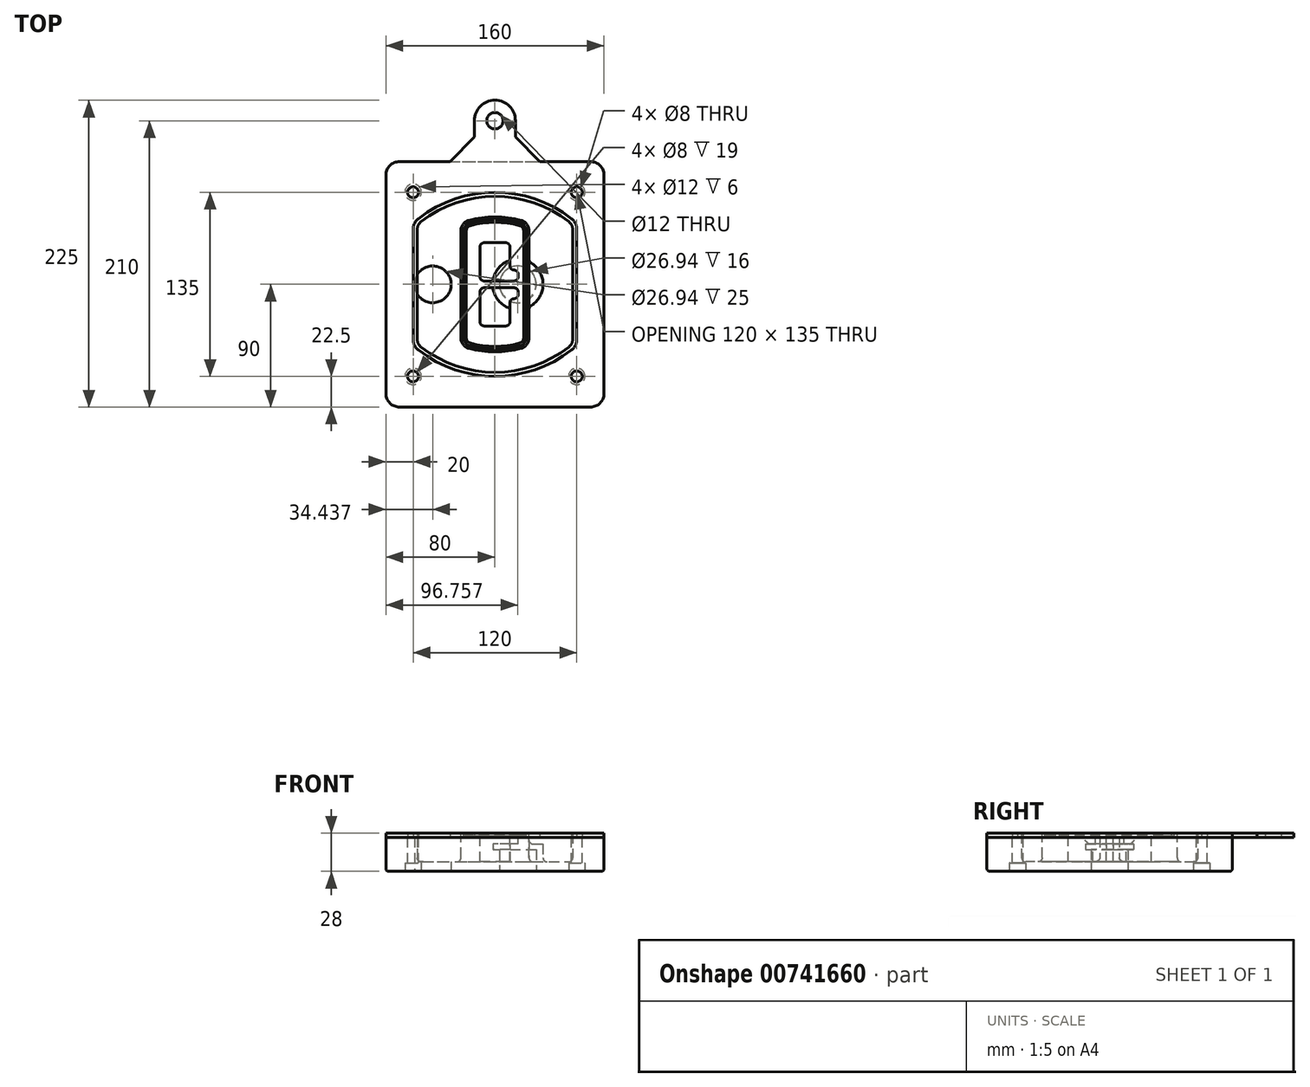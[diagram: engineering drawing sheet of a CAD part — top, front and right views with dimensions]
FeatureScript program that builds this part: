
annotation { "Feature Type Name" : "Feature", "Feature Type Description" : "" }
export const myFeature = defineFeature(function(context is Context, id is Id, definition is map)
    precondition{}
    {
        {
            var Q0;
            Q0=qCreatedBy(makeId("Top.planeOp"),FACE);
            var sketch = newSketch(context, id + "F0", { "sketchPlane" : qUnion([Q0])});
            skPoint(sketch, "E0.rect.middle", {"position": v(0, 0) * mm});
            skLineSegment(sketch, "E1.bottom", {"start": v(-70, -90) * mm, "end": v(70, -90) * mm});
            skLineSegment(sketch, "E1.top", {"start": v(-70, 90) * mm, "end": v(70, 90) * mm});
            skLineSegment(sketch, "E1.left", {"start": v(-80, -80) * mm, "end": v(-80, 80) * mm});
            skLineSegment(sketch, "E1.right", {"start": v(80, -80) * mm, "end": v(80, 80) * mm});
            skLineSegment(sketch, "E2", {"start": v(-80, 90) * mm, "end": v(80, -90) * mm, "construction": true});
            skLineSegment(sketch, "E3", {"start": v(80, 90) * mm, "end": v(-80, -90) * mm, "construction": true});
            skCircle(sketch, "E4", {"center": v(-60, 67.5) * mm, "radius": 4 * mm});
            skCircle(sketch, "E5", {"center": v(60, 67.5) * mm, "radius": 4 * mm});
            skCircle(sketch, "E6", {"center": v(60, -67.5) * mm, "radius": 4 * mm});
            skCircle(sketch, "E7", {"center": v(-60, -67.5) * mm, "radius": 4 * mm});
            skLineSegment(sketch, "E8", {"start": v(-60, 67.5) * mm, "end": v(60, 67.5) * mm, "construction": true});
            skLineSegment(sketch, "E9", {"start": v(60, 67.5) * mm, "end": v(60, -67.5) * mm, "construction": true});
            skLineSegment(sketch, "E10", {"start": v(60, -67.5) * mm, "end": v(-60, -67.5) * mm, "construction": true});
            skLineSegment(sketch, "E11", {"start": v(-60, -67.5) * mm, "end": v(-60, 67.5) * mm, "construction": true});
            skLineSegment(sketch, "E12", {"start": v(-60, 40.3) * mm, "end": v(-60, -40.3) * mm});
            skLineSegment(sketch, "E13", {"start": v(60, 40.3) * mm, "end": v(60, -40.3) * mm});
            skArc(sketch, "E14", {"start": v(56.15, 48.18) * mm, "mid": v(0, 67.5) * mm, "end": v(-56.15, 48.18) * mm});
            skArc(sketch, "E15", {"start": v(-56.15, -48.18) * mm, "mid": v(0, -67.5) * mm, "end": v(56.15, -48.18) * mm});
            skLineSegment(sketch, "E16", {"start": v(-60, 0) * mm, "end": v(60, 0) * mm, "construction": true});
            skPoint(sketch, "E17.visualSharp", {"position": v(-60, -45) * mm});
            skArc(sketch, "E17.filletArc", {"start": v(-60, -40.3) * mm, "mid": v(-58.99, -44.68) * mm, "end": v(-56.15, -48.18) * mm});
            skPoint(sketch, "E18.visualSharp", {"position": v(-60, 45) * mm});
            skArc(sketch, "E18.filletArc", {"start": v(-56.15, 48.18) * mm, "mid": v(-58.99, 44.68) * mm, "end": v(-60, 40.3) * mm});
            skPoint(sketch, "E19.visualSharp", {"position": v(60, 45) * mm});
            skArc(sketch, "E19.filletArc", {"start": v(60, 40.3) * mm, "mid": v(58.99, 44.68) * mm, "end": v(56.15, 48.18) * mm});
            skPoint(sketch, "E20.visualSharp", {"position": v(60, -45) * mm});
            skArc(sketch, "E20.filletArc", {"start": v(56.15, -48.18) * mm, "mid": v(58.99, -44.68) * mm, "end": v(60, -40.3) * mm});
            skPoint(sketch, "E21.visualSharp", {"position": v(-80, 90) * mm});
            skArc(sketch, "E21.filletArc", {"start": v(-70, 90) * mm, "mid": v(-77.07, 87.07) * mm, "end": v(-80, 80) * mm});
            skPoint(sketch, "E22.visualSharp", {"position": v(80, 90) * mm});
            skArc(sketch, "E22.filletArc", {"start": v(80, 80) * mm, "mid": v(77.07, 87.07) * mm, "end": v(70, 90) * mm});
            skPoint(sketch, "E23.visualSharp", {"position": v(80, -90) * mm});
            skArc(sketch, "E23.filletArc", {"start": v(70, -90) * mm, "mid": v(77.07, -87.07) * mm, "end": v(80, -80) * mm});
            skPoint(sketch, "E24.visualSharp", {"position": v(-80, -90) * mm});
            skArc(sketch, "E24.filletArc", {"start": v(-80, -80) * mm, "mid": v(-77.07, -87.07) * mm, "end": v(-70, -90) * mm});
            skArc(sketch, "E25.0", {"start": v(57, 40.3) * mm, "mid": v(56.3, 43.36) * mm, "end": v(54.3, 45.81) * mm});
            skLineSegment(sketch, "E25.1", {"start": v(57, 40.3) * mm, "end": v(57, -40.3) * mm});
            skArc(sketch, "E25.2", {"start": v(54.3, -45.81) * mm, "mid": v(56.3, -43.36) * mm, "end": v(57, -40.3) * mm});
            skArc(sketch, "E25.3", {"start": v(-54.3, -45.81) * mm, "mid": v(0, -64.5) * mm, "end": v(54.3, -45.81) * mm});
            skArc(sketch, "E25.4", {"start": v(-57, -40.3) * mm, "mid": v(-56.3, -43.36) * mm, "end": v(-54.3, -45.81) * mm});
            skArc(sketch, "E25.5", {"start": v(54.3, 45.81) * mm, "mid": v(0, 64.5) * mm, "end": v(-54.3, 45.81) * mm});
            skLineSegment(sketch, "E25.6", {"start": v(-57, 40.3) * mm, "end": v(-57, -40.3) * mm});
            skArc(sketch, "E25.7", {"start": v(-54.3, 45.81) * mm, "mid": v(-56.3, 43.36) * mm, "end": v(-57, 40.3) * mm});
            skArc(sketch, "E26.0", {"start": v(-58.62, 51.33) * mm, "mid": v(-62.58, 46.43) * mm, "end": v(-64, 40.3) * mm});
            skArc(sketch, "E26.1", {"start": v(58.62, 51.33) * mm, "mid": v(0, 71.5) * mm, "end": v(-58.62, 51.33) * mm});
            skArc(sketch, "E26.2", {"start": v(64, 40.3) * mm, "mid": v(62.58, 46.43) * mm, "end": v(58.62, 51.33) * mm});
            skLineSegment(sketch, "E26.3", {"start": v(64, 40.3) * mm, "end": v(64, -40.3) * mm});
            skArc(sketch, "E26.4", {"start": v(58.62, -51.33) * mm, "mid": v(62.58, -46.43) * mm, "end": v(64, -40.3) * mm});
            skLineSegment(sketch, "E26.5", {"start": v(-64, 40.3) * mm, "end": v(-64, -40.3) * mm});
            skArc(sketch, "E26.6", {"start": v(-58.62, -51.33) * mm, "mid": v(0, -71.5) * mm, "end": v(58.62, -51.33) * mm});
            skArc(sketch, "E26.7", {"start": v(-64, -40.3) * mm, "mid": v(-62.58, -46.43) * mm, "end": v(-58.62, -51.33) * mm});
            skSolve(sketch);
        }
        {
            var Q0;
            Q0=makeQuery(id+"F0.imprint","IMPRINT",FACE,{"disambiguationData":[TD([[makeQuery(id+"F0.imprint","IMPRINT",EDGE,{"derivedFrom":sQuery(id+"F0.wireOp",EDGE,"E1.bottom")}),1.0]])]});
            var Q1;
            Q1=makeQuery(id+"F0.imprint","IMPRINT",FACE,{"disambiguationData":[TD([[makeQuery(id+"F0.imprint","IMPRINT",EDGE,{"derivedFrom":sQuery(id+"F0.wireOp",EDGE,"E12")}),1.0]])]});
            var Q2;
            Q2=makeQuery(id+"F0.imprint","IMPRINT",FACE,{"disambiguationData":[TD([[makeQuery(id+"F0.imprint","IMPRINT",EDGE,{"derivedFrom":sQuery(id+"F0.wireOp",EDGE,"E25.0")}),1.0]])]});
            var Q3;
            Q3=makeQuery(id+"F0.imprint","IMPRINT",FACE,{"disambiguationData":[TD([[makeQuery(id+"F0.imprint","IMPRINT",EDGE,{"derivedFrom":sQuery(id+"F0.wireOp",EDGE,"E12")}),-1.0]])]});
            extrude(context, id + "F1", {"entities" : qUnion([Q0, Q1, Q2, Q3]), "oppositeDirection" : true, "depth" : 25 * mm});
        }
        {
            var Q0;
            Q0=makeQuery(id+"F0.imprint","IMPRINT",FACE,{"disambiguationData":[TD([[makeQuery(id+"F0.imprint","IMPRINT",EDGE,{"derivedFrom":sQuery(id+"F0.wireOp",EDGE,"E12")}),1.0]])]});
            extrude(context, id + "F2", {"entities" : qUnion([Q0]), "operationType" : NewBodyOperationType.ADD, "depth" : 3 * mm});
        }
        {
            var Q0;
            Q0=makeQuery(id+"F0.imprint","IMPRINT",FACE,{"disambiguationData":[TD([[makeQuery(id+"F0.imprint","IMPRINT",EDGE,{"derivedFrom":sQuery(id+"F0.wireOp",EDGE,"E25.0")}),1.0]])]});
            extrude(context, id + "F3", {"entities" : qUnion([Q0]), "operationType" : NewBodyOperationType.REMOVE, "oppositeDirection" : true, "depth" : 18 * mm});
        }
        {
            var Q0;
            Q0=makeQuery(id+"F2.opExtrude","CAP_FACE",FACE,{"disambiguationData":[OSD([sQuery(id+"F0.wireOp",EDGE,"E12"),sQuery(id+"F0.wireOp",EDGE,"E13"),sQuery(id+"F0.wireOp",EDGE,"E14"),sQuery(id+"F0.wireOp",EDGE,"E15"),sQuery(id+"F0.wireOp",EDGE,"E17.filletArc"),sQuery(id+"F0.wireOp",EDGE,"E18.filletArc"),sQuery(id+"F0.wireOp",EDGE,"E19.filletArc"),sQuery(id+"F0.wireOp",EDGE,"E20.filletArc"),sQuery(id+"F0.wireOp",EDGE,"E25.0"),sQuery(id+"F0.wireOp",EDGE,"E25.1"),sQuery(id+"F0.wireOp",EDGE,"E25.2"),sQuery(id+"F0.wireOp",EDGE,"E25.3"),sQuery(id+"F0.wireOp",EDGE,"E25.4"),sQuery(id+"F0.wireOp",EDGE,"E25.5"),sQuery(id+"F0.wireOp",EDGE,"E25.6"),sQuery(id+"F0.wireOp",EDGE,"E25.7")])],"isStart":false});
            var sketch = newSketch(context, id + "F4", { "sketchPlane" : qUnion([Q0])});
            skArc(sketch, "E27.0", {"start": v(-19.08, -46.97) * mm, "mid": v(0, -49.5) * mm, "end": v(19.08, -46.97) * mm});
            skArc(sketch, "E28.0", {"start": v(19.08, 46.97) * mm, "mid": v(0, 49.5) * mm, "end": v(-19.08, 46.97) * mm});
            skLineSegment(sketch, "E29", {"start": v(-25, 39.25) * mm, "end": v(-25, -39.25) * mm});
            skLineSegment(sketch, "E30", {"start": v(25, 39.25) * mm, "end": v(25, -39.25) * mm});
            skLineSegment(sketch, "E31", {"start": v(-25, 45.1) * mm, "end": v(25, 45.1) * mm, "construction": true});
            skLineSegment(sketch, "E32", {"start": v(-25, -45.1) * mm, "end": v(25, -45.1) * mm, "construction": true});
            skPoint(sketch, "E33.visualSharp", {"position": v(-25, 45.1) * mm});
            skArc(sketch, "E33.filletArc", {"start": v(-19.08, 46.97) * mm, "mid": v(-23.35, 44.11) * mm, "end": v(-25, 39.25) * mm});
            skPoint(sketch, "E34.visualSharp", {"position": v(25, 45.1) * mm});
            skArc(sketch, "E34.filletArc", {"start": v(25, 39.25) * mm, "mid": v(23.35, 44.11) * mm, "end": v(19.08, 46.97) * mm});
            skPoint(sketch, "E35.visualSharp", {"position": v(25, -45.1) * mm});
            skArc(sketch, "E35.filletArc", {"start": v(19.08, -46.97) * mm, "mid": v(23.35, -44.11) * mm, "end": v(25, -39.25) * mm});
            skPoint(sketch, "E36.visualSharp", {"position": v(-25, -45.1) * mm});
            skArc(sketch, "E36.filletArc", {"start": v(-25, -39.25) * mm, "mid": v(-23.35, -44.11) * mm, "end": v(-19.08, -46.97) * mm});
            skArc(sketch, "E37.0", {"start": v(54.3, 45.81) * mm, "mid": v(0, 64.5) * mm, "end": v(-54.3, 45.81) * mm});
            skArc(sketch, "E37.1", {"start": v(-54.3, 45.81) * mm, "mid": v(-56.3, 43.36) * mm, "end": v(-57, 40.3) * mm});
            skLineSegment(sketch, "E37.2", {"start": v(-57, 40.3) * mm, "end": v(-57, -40.3) * mm});
            skArc(sketch, "E37.3", {"start": v(-57, -40.3) * mm, "mid": v(-56.3, -43.36) * mm, "end": v(-54.3, -45.81) * mm});
            skArc(sketch, "E37.4", {"start": v(-54.3, -45.81) * mm, "mid": v(0, -64.5) * mm, "end": v(54.3, -45.81) * mm});
            skArc(sketch, "E37.5", {"start": v(54.3, -45.81) * mm, "mid": v(56.3, -43.36) * mm, "end": v(57, -40.3) * mm});
            skLineSegment(sketch, "E37.6", {"start": v(57, 40.3) * mm, "end": v(57, -40.3) * mm});
            skArc(sketch, "E37.7", {"start": v(57, 40.3) * mm, "mid": v(56.3, 43.36) * mm, "end": v(54.3, 45.81) * mm});
            skLineSegment(sketch, "E38.0", {"start": v(23, 39.25) * mm, "end": v(23, -39.25) * mm});
            skArc(sketch, "E38.1", {"start": v(18.56, -45.04) * mm, "mid": v(21.76, -42.9) * mm, "end": v(23, -39.25) * mm});
            skArc(sketch, "E38.2", {"start": v(-18.56, -45.04) * mm, "mid": v(0, -47.5) * mm, "end": v(18.56, -45.04) * mm});
            skArc(sketch, "E38.3", {"start": v(-23, -39.25) * mm, "mid": v(-21.76, -42.9) * mm, "end": v(-18.56, -45.04) * mm});
            skLineSegment(sketch, "E38.4", {"start": v(-23, 39.25) * mm, "end": v(-23, -39.25) * mm});
            skArc(sketch, "E38.5", {"start": v(23, 39.25) * mm, "mid": v(21.76, 42.9) * mm, "end": v(18.56, 45.04) * mm});
            skArc(sketch, "E38.6", {"start": v(-18.56, 45.04) * mm, "mid": v(-21.76, 42.9) * mm, "end": v(-23, 39.25) * mm});
            skArc(sketch, "E38.7", {"start": v(18.56, 45.04) * mm, "mid": v(0, 47.5) * mm, "end": v(-18.56, 45.04) * mm});
            skArc(sketch, "E39.0", {"start": v(21, 39.25) * mm, "mid": v(20.18, 41.68) * mm, "end": v(18.04, 43.1) * mm});
            skLineSegment(sketch, "E39.1", {"start": v(21, 39.25) * mm, "end": v(21, -39.25) * mm});
            skArc(sketch, "E39.2", {"start": v(18.04, -43.1) * mm, "mid": v(20.18, -41.68) * mm, "end": v(21, -39.25) * mm});
            skArc(sketch, "E39.3", {"start": v(-18.04, -43.1) * mm, "mid": v(0, -45.5) * mm, "end": v(18.04, -43.1) * mm});
            skArc(sketch, "E39.4", {"start": v(-21, -39.25) * mm, "mid": v(-20.18, -41.68) * mm, "end": v(-18.04, -43.1) * mm});
            skArc(sketch, "E39.5", {"start": v(18.04, 43.1) * mm, "mid": v(0, 45.5) * mm, "end": v(-18.04, 43.1) * mm});
            skLineSegment(sketch, "E39.6", {"start": v(-21, 39.25) * mm, "end": v(-21, -39.25) * mm});
            skArc(sketch, "E39.7", {"start": v(-18.04, 43.1) * mm, "mid": v(-20.18, 41.68) * mm, "end": v(-21, 39.25) * mm});
            skLineSegment(sketch, "E40", {"start": v(-25, 0) * mm, "end": v(25, 0) * mm, "construction": true});
            skLineSegment(sketch, "E41", {"start": v(-11, 5.5) * mm, "end": v(-11, 27.5) * mm});
            skLineSegment(sketch, "E42", {"start": v(-8, 30.5) * mm, "end": v(8, 30.5) * mm});
            skLineSegment(sketch, "E43", {"start": v(11, 27.5) * mm, "end": v(11, 13.5) * mm});
            skLineSegment(sketch, "E44", {"start": v(14, 10.5) * mm, "end": v(14, 10.5) * mm});
            skLineSegment(sketch, "E45", {"start": v(17, 7.5) * mm, "end": v(17, 5.5) * mm});
            skLineSegment(sketch, "E46", {"start": v(14, 2.5) * mm, "end": v(-8, 2.5) * mm});
            skPoint(sketch, "E47.visualSharp", {"position": v(-11, 30.5) * mm});
            skArc(sketch, "E47.filletArc", {"start": v(-8, 30.5) * mm, "mid": v(-10.12, 29.62) * mm, "end": v(-11, 27.5) * mm});
            skPoint(sketch, "E48.visualSharp", {"position": v(11, 30.5) * mm});
            skArc(sketch, "E48.filletArc", {"start": v(11, 27.5) * mm, "mid": v(10.12, 29.62) * mm, "end": v(8, 30.5) * mm});
            skPoint(sketch, "E49.visualSharp", {"position": v(11, 10.5) * mm});
            skArc(sketch, "E49.filletArc", {"start": v(11, 13.5) * mm, "mid": v(11.88, 11.38) * mm, "end": v(14, 10.5) * mm});
            skPoint(sketch, "E50.visualSharp", {"position": v(17, 10.5) * mm});
            skArc(sketch, "E50.filletArc", {"start": v(17, 7.5) * mm, "mid": v(16.12, 9.62) * mm, "end": v(14, 10.5) * mm});
            skPoint(sketch, "E51.visualSharp", {"position": v(17, 2.5) * mm});
            skArc(sketch, "E51.filletArc", {"start": v(14, 2.5) * mm, "mid": v(16.12, 3.38) * mm, "end": v(17, 5.5) * mm});
            skPoint(sketch, "E52.visualSharp", {"position": v(-11, 2.5) * mm});
            skArc(sketch, "E52.filletArc", {"start": v(-11, 5.5) * mm, "mid": v(-10.12, 3.38) * mm, "end": v(-8, 2.5) * mm});
            skLineSegment(sketch, "E53.0.MirrorCS", {"start": v(14, -2.5) * mm, "end": v(-8, -2.5) * mm});
            skArc(sketch, "E54.0.MirrorCS", {"start": v(-11, -5.5) * mm, "mid": v(-10.12, -3.38) * mm, "end": v(-8, -2.5) * mm});
            skLineSegment(sketch, "E55.0.MirrorCS", {"start": v(-11, -5.5) * mm, "end": v(-11, -27.5) * mm});
            skArc(sketch, "E56.0.MirrorCS", {"start": v(-8, -30.5) * mm, "mid": v(-10.12, -29.62) * mm, "end": v(-11, -27.5) * mm});
            skLineSegment(sketch, "E57.0.MirrorCS", {"start": v(-8, -30.5) * mm, "end": v(8, -30.5) * mm});
            skArc(sketch, "E58.0.MirrorCS", {"start": v(11, -27.5) * mm, "mid": v(10.12, -29.62) * mm, "end": v(8, -30.5) * mm});
            skLineSegment(sketch, "E59.0.MirrorCS", {"start": v(11, -27.5) * mm, "end": v(11, -13.5) * mm});
            skArc(sketch, "E60.0.MirrorCS", {"start": v(11, -13.5) * mm, "mid": v(11.88, -11.38) * mm, "end": v(14, -10.5) * mm});
            skArc(sketch, "E61.0.MirrorCS", {"start": v(17, -7.5) * mm, "mid": v(16.12, -9.62) * mm, "end": v(14, -10.5) * mm});
            skLineSegment(sketch, "E62.0.MirrorCS", {"start": v(17, -7.5) * mm, "end": v(17, -5.5) * mm});
            skArc(sketch, "E63.0.MirrorCS", {"start": v(14, -2.5) * mm, "mid": v(16.12, -3.38) * mm, "end": v(17, -5.5) * mm});
            skSolve(sketch);
        }
        {
            var Q0;
            Q0=makeQuery(id+"F4.imprint","IMPRINT",FACE,{"disambiguationData":[TD([[makeQuery(id+"F4.imprint","IMPRINT",EDGE,{"derivedFrom":sQuery(id+"F4.wireOp",EDGE,"E27.0")}),1.0]])]});
            var Q1;
            Q1=makeQuery(id+"F4.imprint","IMPRINT",FACE,{"disambiguationData":[TD([[makeQuery(id+"F4.imprint","IMPRINT",EDGE,{"derivedFrom":sQuery(id+"F4.wireOp",EDGE,"E38.0")}),-1.0]])]});
            var Q2;
            Q2=makeQuery(id+"F4.imprint","IMPRINT",FACE,{"disambiguationData":[TD([[makeQuery(id+"F4.imprint","IMPRINT",EDGE,{"derivedFrom":sQuery(id+"F4.wireOp",EDGE,"E39.0")}),1.0]])]});
            extrude(context, id + "F5", {"entities" : qUnion([Q0, Q1, Q2]), "operationType" : NewBodyOperationType.ADD, "endBound" : BoundingType.UP_TO_NEXT, "oppositeDirection" : true, "depth" : 25 * mm});
        }
        {
            var Q0;
            Q0=makeQuery(id+"F4.imprint","IMPRINT",FACE,{"disambiguationData":[TD([[makeQuery(id+"F4.imprint","IMPRINT",EDGE,{"derivedFrom":sQuery(id+"F4.wireOp",EDGE,"E38.0")}),-1.0]])]});
            extrude(context, id + "F6", {"entities" : qUnion([Q0]), "operationType" : NewBodyOperationType.REMOVE, "oppositeDirection" : true, "depth" : 2 * mm});
        }
        {
            var Q0;
            Q0=makeQuery(id+"F1.opExtrude","CAP_FACE",FACE,{"disambiguationData":[OSD([sQuery(id+"F0.wireOp",EDGE,"E1.bottom"),sQuery(id+"F0.wireOp",EDGE,"E1.top"),sQuery(id+"F0.wireOp",EDGE,"E1.left"),sQuery(id+"F0.wireOp",EDGE,"E1.right"),sQuery(id+"F0.wireOp",EDGE,"E4"),sQuery(id+"F0.wireOp",EDGE,"E5"),sQuery(id+"F0.wireOp",EDGE,"E6"),sQuery(id+"F0.wireOp",EDGE,"E7"),sQuery(id+"F0.wireOp",EDGE,"E21.filletArc"),sQuery(id+"F0.wireOp",EDGE,"E22.filletArc"),sQuery(id+"F0.wireOp",EDGE,"E23.filletArc"),sQuery(id+"F0.wireOp",EDGE,"E24.filletArc")])],"isStart":false});
            var sketch = newSketch(context, id + "F7", { "sketchPlane" : qUnion([Q0])});
            skCircle(sketch, "E64", {"center": v(16.76, 0) * mm, "radius": 13.47 * mm});
            skCircle(sketch, "E65", {"center": v(-45.56, 0) * mm, "radius": 13.47 * mm});
            skLineSegment(sketch, "E66", {"start": v(80, 0) * mm, "end": v(-80, 0) * mm});
            skCircle(sketch, "E67", {"center": v(16.76, 0) * mm, "radius": 18.47 * mm});
            skCircle(sketch, "E68", {"center": v(60, -67.5) * mm, "radius": 6 * mm});
            skCircle(sketch, "E69", {"center": v(-60, -67.5) * mm, "radius": 6 * mm});
            skCircle(sketch, "E70", {"center": v(-60, 67.5) * mm, "radius": 6 * mm});
            skCircle(sketch, "E71", {"center": v(60, 67.5) * mm, "radius": 6 * mm});
            skSolve(sketch);
        }
        {
            var Q0;
            {var subQ1=sQuery(id+"F7.wireOp",EDGE,"E66");var subQ4=sQuery(id+"F7.wireOp",EDGE,"E64");var subQ6=makeQuery(id+"F7.imprint","INTERSECT",VERTEX,{"disambiguationData":[OD(0.0)],"derivedFrom":[subQ4,subQ1]});Q0=makeQuery(id+"F7.imprint","IMPRINT",FACE,{"disambiguationData":[TD([[makeQuery(id+"F7.imprint","IMPRINT",EDGE,{"disambiguationData":[TD([[subQ6,-1.0]])],"derivedFrom":subQ4}),-1.0]])]});}
            var Q1;
            {var subQ0=sQuery(id+"F7.wireOp",EDGE,"E66");var subQ1=sQuery(id+"F7.wireOp",EDGE,"E64");var subQ3=makeQuery(id+"F7.imprint","INTERSECT",VERTEX,{"disambiguationData":[OD(0.0)],"derivedFrom":[subQ1,subQ0]});Q1=makeQuery(id+"F7.imprint","IMPRINT",FACE,{"disambiguationData":[TD([[makeQuery(id+"F7.imprint","IMPRINT",EDGE,{"disambiguationData":[TD([[subQ3,-1.0]])],"derivedFrom":subQ1}),1.0]])]});}
            var Q2;
            {var subQ0=sQuery(id+"F7.wireOp",EDGE,"E66");var subQ1=sQuery(id+"F7.wireOp",EDGE,"E64");var subQ3=makeQuery(id+"F7.imprint","INTERSECT",VERTEX,{"disambiguationData":[OD(0.0)],"derivedFrom":[subQ1,subQ0]});Q2=makeQuery(id+"F7.imprint","IMPRINT",FACE,{"disambiguationData":[TD([[makeQuery(id+"F7.imprint","IMPRINT",EDGE,{"disambiguationData":[TD([[subQ3,1.0]])],"derivedFrom":subQ1}),1.0]])]});}
            var Q3;
            {var subQ1=sQuery(id+"F7.wireOp",EDGE,"E66");var subQ4=sQuery(id+"F7.wireOp",EDGE,"E64");var subQ6=makeQuery(id+"F7.imprint","INTERSECT",VERTEX,{"disambiguationData":[OD(0.0)],"derivedFrom":[subQ4,subQ1]});Q3=makeQuery(id+"F7.imprint","IMPRINT",FACE,{"disambiguationData":[TD([[makeQuery(id+"F7.imprint","IMPRINT",EDGE,{"disambiguationData":[TD([[subQ6,1.0]])],"derivedFrom":subQ4}),-1.0]])]});}
            extrude(context, id + "F8", {"entities" : qUnion([Q0, Q1, Q2, Q3]), "operationType" : NewBodyOperationType.ADD, "oppositeDirection" : true, "depth" : 20 * mm});
        }
        {
            var Q0;
            {var subQ0=sQuery(id+"F7.wireOp",EDGE,"E66");var subQ1=sQuery(id+"F7.wireOp",EDGE,"E64");var subQ3=makeQuery(id+"F7.imprint","INTERSECT",VERTEX,{"disambiguationData":[OD(0.0)],"derivedFrom":[subQ1,subQ0]});Q0=makeQuery(id+"F7.imprint","IMPRINT",FACE,{"disambiguationData":[TD([[makeQuery(id+"F7.imprint","IMPRINT",EDGE,{"disambiguationData":[TD([[subQ3,-1.0]])],"derivedFrom":subQ1}),1.0]])]});}
            var Q1;
            {var subQ0=sQuery(id+"F7.wireOp",EDGE,"E66");var subQ1=sQuery(id+"F7.wireOp",EDGE,"E64");var subQ3=makeQuery(id+"F7.imprint","INTERSECT",VERTEX,{"disambiguationData":[OD(0.0)],"derivedFrom":[subQ1,subQ0]});Q1=makeQuery(id+"F7.imprint","IMPRINT",FACE,{"disambiguationData":[TD([[makeQuery(id+"F7.imprint","IMPRINT",EDGE,{"disambiguationData":[TD([[subQ3,1.0]])],"derivedFrom":subQ1}),1.0]])]});}
            extrude(context, id + "F9", {"entities" : qUnion([Q0, Q1]), "operationType" : NewBodyOperationType.REMOVE, "oppositeDirection" : true, "depth" : 16 * mm});
        }
        {
            var Q0;
            {var subQ0=sQuery(id+"F7.wireOp",EDGE,"E66");var subQ1=sQuery(id+"F7.wireOp",EDGE,"E65");var subQ3=makeQuery(id+"F7.imprint","INTERSECT",VERTEX,{"disambiguationData":[OD(0.0)],"derivedFrom":[subQ1,subQ0]});Q0=makeQuery(id+"F7.imprint","IMPRINT",FACE,{"disambiguationData":[TD([[makeQuery(id+"F7.imprint","IMPRINT",EDGE,{"disambiguationData":[TD([[subQ3,-1.0]])],"derivedFrom":subQ1}),1.0]])]});}
            var Q1;
            {var subQ0=sQuery(id+"F7.wireOp",EDGE,"E66");var subQ1=sQuery(id+"F7.wireOp",EDGE,"E65");var subQ3=makeQuery(id+"F7.imprint","INTERSECT",VERTEX,{"disambiguationData":[OD(0.0)],"derivedFrom":[subQ1,subQ0]});Q1=makeQuery(id+"F7.imprint","IMPRINT",FACE,{"disambiguationData":[TD([[makeQuery(id+"F7.imprint","IMPRINT",EDGE,{"disambiguationData":[TD([[subQ3,1.0]])],"derivedFrom":subQ1}),1.0]])]});}
            extrude(context, id + "F10", {"entities" : qUnion([Q0, Q1]), "operationType" : NewBodyOperationType.REMOVE, "oppositeDirection" : true, "depth" : 25 * mm});
        }
        {
            var Q0;
            Q0=makeQuery(id+"F7.imprint","IMPRINT",FACE,{"disambiguationData":[TD([[makeQuery(id+"F7.imprint","IMPRINT",EDGE,{"derivedFrom":sQuery(id+"F7.wireOp",EDGE,"E68")}),1.0]])]});
            var Q1;
            Q1=makeQuery(id+"F7.imprint","IMPRINT",FACE,{"disambiguationData":[TD([[makeQuery(id+"F7.imprint","IMPRINT",EDGE,{"derivedFrom":makeQuery(id+"F1.opExtrude","CAP_EDGE",EDGE,{"disambiguationData":[OSD([sQuery(id+"F0.wireOp",EDGE,"E5")])],"isStart":false})}),-1.0]])]});
            var Q2;
            Q2=makeQuery(id+"F7.imprint","IMPRINT",FACE,{"disambiguationData":[TD([[makeQuery(id+"F7.imprint","IMPRINT",EDGE,{"derivedFrom":sQuery(id+"F7.wireOp",EDGE,"E69")}),1.0]])]});
            var Q3;
            Q3=makeQuery(id+"F7.imprint","IMPRINT",FACE,{"disambiguationData":[TD([[makeQuery(id+"F7.imprint","IMPRINT",EDGE,{"derivedFrom":makeQuery(id+"F1.opExtrude","CAP_EDGE",EDGE,{"disambiguationData":[OSD([sQuery(id+"F0.wireOp",EDGE,"E4")])],"isStart":false})}),-1.0]])]});
            var Q4;
            Q4=makeQuery(id+"F7.imprint","IMPRINT",FACE,{"disambiguationData":[TD([[makeQuery(id+"F7.imprint","IMPRINT",EDGE,{"derivedFrom":sQuery(id+"F7.wireOp",EDGE,"E70")}),1.0]])]});
            var Q5;
            Q5=makeQuery(id+"F7.imprint","IMPRINT",FACE,{"disambiguationData":[TD([[makeQuery(id+"F7.imprint","IMPRINT",EDGE,{"derivedFrom":makeQuery(id+"F1.opExtrude","CAP_EDGE",EDGE,{"disambiguationData":[OSD([sQuery(id+"F0.wireOp",EDGE,"E7")])],"isStart":false})}),-1.0]])]});
            var Q6;
            Q6=makeQuery(id+"F7.imprint","IMPRINT",FACE,{"disambiguationData":[TD([[makeQuery(id+"F7.imprint","IMPRINT",EDGE,{"derivedFrom":sQuery(id+"F7.wireOp",EDGE,"E71")}),1.0]])]});
            var Q7;
            Q7=makeQuery(id+"F7.imprint","IMPRINT",FACE,{"disambiguationData":[TD([[makeQuery(id+"F7.imprint","IMPRINT",EDGE,{"derivedFrom":makeQuery(id+"F1.opExtrude","CAP_EDGE",EDGE,{"disambiguationData":[OSD([sQuery(id+"F0.wireOp",EDGE,"E6")])],"isStart":false})}),-1.0]])]});
            extrude(context, id + "F11", {"entities" : qUnion([Q0, Q1, Q2, Q3, Q4, Q5, Q6, Q7]), "operationType" : NewBodyOperationType.REMOVE, "oppositeDirection" : true, "depth" : 6 * mm});
        }
        {
            var Q0;
            Q0=makeQuery(id+"F9.boolean.opBoolean","COPY",FACE,{"derivedFrom":makeQuery(id+"F9.opExtrude","CAP_FACE",FACE,{"disambiguationData":[OSD([sQuery(id+"F7.wireOp",EDGE,"E64")])],"isStart":false})});
            var sketch = newSketch(context, id + "F12", { "sketchPlane" : qUnion([Q0])});
            skArc(sketch, "E72.0", {"start": v(11, 17.55) * mm, "mid": v(2.57, 11.82) * mm, "end": v(-1.54, 2.5) * mm});
            skArc(sketch, "E72.1", {"start": v(-1.54, -2.5) * mm, "mid": v(2.57, -11.82) * mm, "end": v(11, -17.55) * mm});
            skLineSegment(sketch, "E73", {"start": v(-1.54, -2.5) * mm, "end": v(14, -2.5) * mm});
            skLineSegment(sketch, "E74.0", {"start": v(14, 2.5) * mm, "end": v(-1.54, 2.5) * mm});
            skArc(sketch, "E74.1", {"start": v(14, 2.5) * mm, "mid": v(16.12, 3.38) * mm, "end": v(17, 5.5) * mm});
            skLineSegment(sketch, "E74.2", {"start": v(17, 7.5) * mm, "end": v(17, 5.5) * mm});
            skArc(sketch, "E74.3", {"start": v(17, 7.5) * mm, "mid": v(16.12, 9.62) * mm, "end": v(14, 10.5) * mm});
            skArc(sketch, "E74.4", {"start": v(11, 13.5) * mm, "mid": v(11.88, 11.38) * mm, "end": v(14, 10.5) * mm});
            skLineSegment(sketch, "E74.5", {"start": v(11, 17.55) * mm, "end": v(11, 13.5) * mm});
            skLineSegment(sketch, "E74.7", {"start": v(14, -2.5) * mm, "end": v(-1.54, -2.5) * mm});
            skArc(sketch, "E74.8", {"start": v(14, -2.5) * mm, "mid": v(16.12, -3.38) * mm, "end": v(17, -5.5) * mm});
            skLineSegment(sketch, "E74.9", {"start": v(17, -7.5) * mm, "end": v(17, -5.5) * mm});
            skArc(sketch, "E74.10", {"start": v(17, -7.5) * mm, "mid": v(16.12, -9.62) * mm, "end": v(14, -10.5) * mm});
            skArc(sketch, "E74.11", {"start": v(11, -13.5) * mm, "mid": v(11.88, -11.38) * mm, "end": v(14, -10.5) * mm});
            skLineSegment(sketch, "E74.12", {"start": v(11, -17.55) * mm, "end": v(11, -13.5) * mm});
            skPoint(sketch, "E75.orphan", {"position": v(11, -27.5) * mm});
            skPoint(sketch, "E76.orphan", {"position": v(-8, -2.5) * mm});
            skPoint(sketch, "E77.orphan", {"position": v(-8, 2.5) * mm});
            skPoint(sketch, "E78.orphan", {"position": v(11, 27.5) * mm});
            skSolve(sketch);
        }
        {
            var Q0;
            {var subQ7=sQuery(id+"F12.wireOp",EDGE,"E72.0");var subQ14=sQuery(id+"F12.wireOp",EDGE,"E72.1");var subQ16=sQuery(id+"F12.wireOp",EDGE,"E74.1");var subQ18=sQuery(id+"F12.wireOp",EDGE,"E74.8");Q0=qUnion([makeQuery(id+"F12.imprint","IMPRINT",FACE,{"disambiguationData":[TD([[makeQuery(id+"F12.imprint","IMPRINT",EDGE,{"derivedFrom":subQ7}),1.0]])]}),makeQuery(id+"F12.imprint","IMPRINT",FACE,{"disambiguationData":[TD([[makeQuery(id+"F12.imprint","IMPRINT",EDGE,{"derivedFrom":subQ14}),1.0]])]}),makeQuery(id+"F12.imprint","IMPRINT",FACE,{"disambiguationData":[TD([[makeQuery(id+"F12.imprint","IMPRINT",EDGE,{"derivedFrom":subQ16}),1.0]])]}),makeQuery(id+"F12.imprint","IMPRINT",FACE,{"disambiguationData":[TD([[makeQuery(id+"F12.imprint","IMPRINT",EDGE,{"derivedFrom":subQ18}),-1.0]])]})]);}
            var Q1;
            Q1=makeQuery(id+"F5.boolean.opBoolean","SPLIT",FACE,{"disambiguationData":[TD([makeQuery(id+"F5.opExtrude","SWEPT_FACE",FACE,{"disambiguationData":[OSD([sQuery(id+"F4.wireOp",EDGE,"E41")])]})])],"derivedFrom":makeQuery(id+"F3.boolean.opBoolean","COPY",FACE,{"derivedFrom":makeQuery(id+"F3.opExtrude","CAP_FACE",FACE,{"disambiguationData":[OSD([sQuery(id+"F0.wireOp",EDGE,"E25.0"),sQuery(id+"F0.wireOp",EDGE,"E25.1"),sQuery(id+"F0.wireOp",EDGE,"E25.2"),sQuery(id+"F0.wireOp",EDGE,"E25.3"),sQuery(id+"F0.wireOp",EDGE,"E25.4"),sQuery(id+"F0.wireOp",EDGE,"E25.5"),sQuery(id+"F0.wireOp",EDGE,"E25.6"),sQuery(id+"F0.wireOp",EDGE,"E25.7")])],"isStart":false})})});
            extrude(context, id + "F13", {"entities" : qUnion([Q0]), "operationType" : NewBodyOperationType.REMOVE, "endBound" : BoundingType.UP_TO_SURFACE, "endBoundEntityFace" : qUnion([Q1]), "depth" : 25 * mm});
        }
        {
            var Q0;
            Q0=makeQuery(id+"F3.boolean.opBoolean","COPY",EDGE,{"derivedFrom":makeQuery(id+"F3.opExtrude","CAP_EDGE",EDGE,{"disambiguationData":[OSD([sQuery(id+"F0.wireOp",EDGE,"E25.6")])],"isStart":false})});
            var Q1;
            Q1=makeQuery(id+"F8.boolean.opBoolean","INTERSECT",EDGE,{"derivedFrom":[makeQuery(id+"F5.opExtrude","SWEPT_FACE",FACE,{"disambiguationData":[OSD([sQuery(id+"F4.wireOp",EDGE,"E30")])]}),makeQuery(id+"F8.opExtrude","CAP_FACE",FACE,{"disambiguationData":[OSD([sQuery(id+"F7.wireOp",EDGE,"E67")])],"isStart":false})]});
            var Q2;
            Q2=makeQuery(id+"F8.boolean.opBoolean","INTERSECT",EDGE,{"disambiguationData":[OD(1.0)],"derivedFrom":[makeQuery(id+"F5.opExtrude","SWEPT_FACE",FACE,{"disambiguationData":[OSD([sQuery(id+"F4.wireOp",EDGE,"E30")])]}),makeQuery(id+"F8.opExtrude","SWEPT_FACE",FACE,{"disambiguationData":[OSD([sQuery(id+"F7.wireOp",EDGE,"E67")])]})]});
            var Q3;
            {var subQ0=sQuery(id+"F4.wireOp",EDGE,"E30");Q3=makeQuery(id+"F8.boolean.opBoolean","SPLIT",EDGE,{"disambiguationData":[TD([makeQuery(id+"F5.opExtrude","SWEPT_FACE",FACE,{"disambiguationData":[OSD([sQuery(id+"F4.wireOp",EDGE,"E35.filletArc")])]})])],"derivedFrom":makeQuery(id+"F5.opExtrude","CAP_EDGE",EDGE,{"disambiguationData":[OSD([subQ0])],"isStart":false})});}
            var Q4;
            {var subQ0=sQuery(id+"F0.wireOp",EDGE,"E25.7");var subQ1=sQuery(id+"F0.wireOp",EDGE,"E25.1");var subQ2=sQuery(id+"F0.wireOp",EDGE,"E25.6");var subQ3=sQuery(id+"F0.wireOp",EDGE,"E25.5");var subQ4=sQuery(id+"F0.wireOp",EDGE,"E25.4");var subQ5=sQuery(id+"F0.wireOp",EDGE,"E25.0");var subQ6=sQuery(id+"F0.wireOp",EDGE,"E25.2");var subQ7=sQuery(id+"F0.wireOp",EDGE,"E25.3");Q4=makeQuery(id+"F8.boolean.opBoolean","INTERSECT",EDGE,{"derivedFrom":[makeQuery(id+"F5.boolean.opBoolean","SPLIT",FACE,{"disambiguationData":[TD([makeQuery(id+"F2.opExtrude","SWEPT_FACE",FACE,{"disambiguationData":[OSD([subQ5])]})])],"derivedFrom":makeQuery(id+"F3.boolean.opBoolean","COPY",FACE,{"derivedFrom":makeQuery(id+"F3.opExtrude","CAP_FACE",FACE,{"disambiguationData":[OSD([subQ5,subQ1,subQ6,subQ7,subQ4,subQ3,subQ2,subQ0])],"isStart":false})})}),makeQuery(id+"F8.opExtrude","SWEPT_FACE",FACE,{"disambiguationData":[OSD([sQuery(id+"F7.wireOp",EDGE,"E67")])]})]});}
            var Q5;
            Q5=makeQuery(id+"F8.boolean.opBoolean","INTERSECT",EDGE,{"disambiguationData":[OD(0.0)],"derivedFrom":[makeQuery(id+"F5.opExtrude","SWEPT_FACE",FACE,{"disambiguationData":[OSD([sQuery(id+"F4.wireOp",EDGE,"E30")])]}),makeQuery(id+"F8.opExtrude","SWEPT_FACE",FACE,{"disambiguationData":[OSD([sQuery(id+"F7.wireOp",EDGE,"E67")])]})]});
            fillet(context, id + "F14", {"entities" : qUnion([Q0, Q1, Q2, Q3, Q4, Q5]), "radius" : 3 * mm, "tangentPropagation" : true, "allowEdgeOverflow" : false});
        }
        {
            var Q0;
            Q0=makeQuery(id+"F1.opExtrude","CAP_EDGE",EDGE,{"disambiguationData":[OSD([sQuery(id+"F0.wireOp",EDGE,"E1.bottom")])],"isStart":false});
            fillet(context, id + "F15", {"entities" : qUnion([Q0]), "radius" : 2 * mm, "tangentPropagation" : true, "allowEdgeOverflow" : false});
        }
        {
            var Q0;
            {var subQ0=sQuery(id+"F0.wireOp",EDGE,"E21.filletArc");var subQ1=sQuery(id+"F0.wireOp",EDGE,"E7");var subQ2=sQuery(id+"F0.wireOp",EDGE,"E6");var subQ3=sQuery(id+"F0.wireOp",EDGE,"E5");var subQ4=sQuery(id+"F0.wireOp",EDGE,"E4");var subQ5=sQuery(id+"F0.wireOp",EDGE,"E22.filletArc");var subQ6=sQuery(id+"F0.wireOp",EDGE,"E1.bottom");var subQ7=sQuery(id+"F0.wireOp",EDGE,"E1.right");var subQ8=sQuery(id+"F0.wireOp",EDGE,"E1.top");var subQ9=sQuery(id+"F0.wireOp",EDGE,"E1.left");var subQ10=sQuery(id+"F0.wireOp",EDGE,"E23.filletArc");var subQ11=sQuery(id+"F0.wireOp",EDGE,"E24.filletArc");Q0=makeQuery(id+"F2.boolean.opBoolean","SPLIT",FACE,{"disambiguationData":[TD([makeQuery(id+"F1.opExtrude","SWEPT_FACE",FACE,{"disambiguationData":[OSD([subQ6])]})])],"derivedFrom":makeQuery(id+"F1.opExtrude","CAP_FACE",FACE,{"disambiguationData":[OSD([subQ6,subQ8,subQ9,subQ7,subQ4,subQ3,subQ2,subQ1,subQ0,subQ5,subQ10,subQ11])],"isStart":true})});}
            var sketch = newSketch(context, id + "F16", { "sketchPlane" : qUnion([Q0])});
            skLineSegment(sketch, "E79", {"start": v(0, 90) * mm, "end": v(0, 120) * mm, "construction": true});
            skCircle(sketch, "E80", {"center": v(0, 120) * mm, "radius": 6 * mm});
            skLineSegment(sketch, "E81", {"start": v(15, 120) * mm, "end": v(15, 108) * mm});
            skLineSegment(sketch, "E82", {"start": v(-15, 108) * mm, "end": v(-15, 120) * mm});
            skLineSegment(sketch, "E83", {"start": v(-15, 108) * mm, "end": v(-33, 90) * mm});
            skLineSegment(sketch, "E84", {"start": v(15, 108) * mm, "end": v(33, 90) * mm});
            skArc(sketch, "E85", {"start": v(15, 120) * mm, "mid": v(0, 135) * mm, "end": v(-15, 120) * mm});
            skLineSegment(sketch, "E86", {"start": v(-80, 0) * mm, "end": v(80, 0) * mm, "construction": true});
            skArc(sketch, "E87.MirrorCS", {"start": v(15, -120) * mm, "mid": v(0, -135) * mm, "end": v(-15, -120) * mm});
            skCircle(sketch, "E88.MirrorC", {"center": v(0, -120) * mm, "radius": 6 * mm});
            skLineSegment(sketch, "E89.MirrorCS", {"start": v(-15, -108) * mm, "end": v(-15, -120) * mm});
            skLineSegment(sketch, "E90.MirrorCS", {"start": v(15, -120) * mm, "end": v(15, -108) * mm});
            skLineSegment(sketch, "E91.MirrorCS", {"start": v(15, -108) * mm, "end": v(33, -90) * mm});
            skLineSegment(sketch, "E92.MirrorCS", {"start": v(-15, -108) * mm, "end": v(-33, -90) * mm});
            skLineSegment(sketch, "E93.MirrorCS", {"start": v(0, -90) * mm, "end": v(0, -120) * mm, "construction": true});
            skSolve(sketch);
        }
        {
            var Q0;
            Q0=makeQuery(id+"F16.imprint","IMPRINT",FACE,{"disambiguationData":[TD([[makeQuery(id+"F16.imprint","IMPRINT",EDGE,{"derivedFrom":sQuery(id+"F16.wireOp",EDGE,"E80")}),-1.0]])]});
            var Q1;
            Q1=makeQuery(id+"F16.imprint","IMPRINT",FACE,{"disambiguationData":[TD([[makeQuery(id+"F16.imprint","IMPRINT",EDGE,{"derivedFrom":sQuery(id+"F16.wireOp",EDGE,"E87.MirrorCS")}),-1.0]])]});
            var Q2;
            Q2=makeQuery(id+"F16.imprint","IMPRINT",FACE,{"disambiguationData":[TD([[makeQuery(id+"F16.imprint","IMPRINT",EDGE,{"derivedFrom":makeQuery(id+"F1.opExtrude","CAP_EDGE",EDGE,{"disambiguationData":[OSD([sQuery(id+"F0.wireOp",EDGE,"E1.left")])],"isStart":true})}),-1.0]])]});
            var Q3;
            Q3=makeQuery(id+"F2.opExtrude","CAP_FACE",FACE,{"disambiguationData":[OSD([sQuery(id+"F0.wireOp",EDGE,"E12"),sQuery(id+"F0.wireOp",EDGE,"E13"),sQuery(id+"F0.wireOp",EDGE,"E14"),sQuery(id+"F0.wireOp",EDGE,"E15"),sQuery(id+"F0.wireOp",EDGE,"E17.filletArc"),sQuery(id+"F0.wireOp",EDGE,"E18.filletArc"),sQuery(id+"F0.wireOp",EDGE,"E19.filletArc"),sQuery(id+"F0.wireOp",EDGE,"E20.filletArc"),sQuery(id+"F0.wireOp",EDGE,"E25.0"),sQuery(id+"F0.wireOp",EDGE,"E25.1"),sQuery(id+"F0.wireOp",EDGE,"E25.2"),sQuery(id+"F0.wireOp",EDGE,"E25.3"),sQuery(id+"F0.wireOp",EDGE,"E25.4"),sQuery(id+"F0.wireOp",EDGE,"E25.5"),sQuery(id+"F0.wireOp",EDGE,"E25.6"),sQuery(id+"F0.wireOp",EDGE,"E25.7")])],"isStart":false});
            extrude(context, id + "F17", {"entities" : qUnion([Q0, Q1, Q2]), "endBound" : BoundingType.UP_TO_SURFACE, "depth" : 25 * mm, "endBoundEntityFace" : qUnion([Q3]), "offsetDistance" : 25 * mm});
        }
    });
